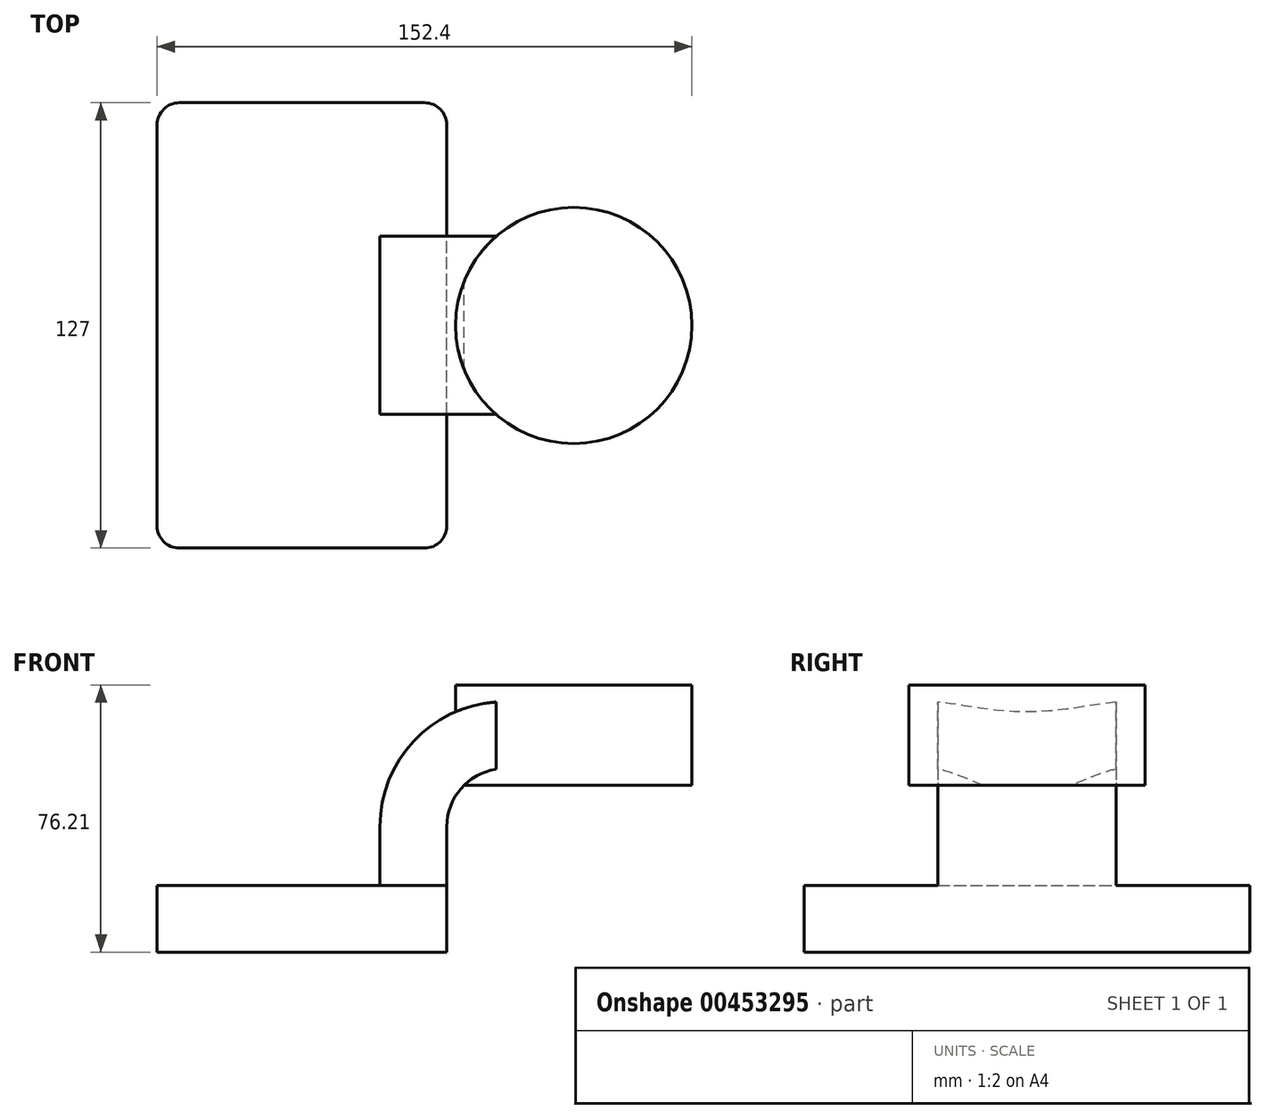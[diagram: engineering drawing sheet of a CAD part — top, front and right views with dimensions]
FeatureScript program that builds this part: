
annotation { "Feature Type Name" : "Feature", "Feature Type Description" : "" }
export const myFeature = defineFeature(function(context is Context, id is Id, definition is map)
    precondition{}
    {
        {
            var Q0;
            Q0=qCreatedBy(makeId("Front.planeOp"),FACE);
            var sketch = newSketch(context, id + "F0", { "sketchPlane" : qUnion([Q0])});
            skLineSegment(sketch, "E0.bottom", {"start": v(41.27, 9.53) * mm, "end": v(-41.27, 9.53) * mm});
            skLineSegment(sketch, "E0.top", {"start": v(41.27, -9.52) * mm, "end": v(-41.27, -9.52) * mm});
            skLineSegment(sketch, "E0.left", {"start": v(41.27, 9.53) * mm, "end": v(41.27, -9.52) * mm});
            skLineSegment(sketch, "E0.right", {"start": v(-41.27, 9.53) * mm, "end": v(-41.27, -9.52) * mm});
            skPoint(sketch, "E0.middle", {"position": v(0, 0) * mm});
            skLineSegment(sketch, "E1", {"start": v(41.27, 9.53) * mm, "end": v(41.27, 26.29) * mm});
            skArc(sketch, "E2", {"start": v(41.27, 26.29) * mm, "mid": v(46.11, 37.96) * mm, "end": v(57.78, 42.8) * mm});
            skLineSegment(sketch, "E3", {"start": v(57.78, 42.8) * mm, "end": v(77.45, 42.8) * mm});
            skLineSegment(sketch, "E4.bottom", {"start": v(111.12, 38.1) * mm, "end": v(60.32, 38.1) * mm});
            skLineSegment(sketch, "E4.top", {"start": v(111.12, 66.68) * mm, "end": v(60.32, 66.68) * mm});
            skLineSegment(sketch, "E4.left", {"start": v(111.12, 38.1) * mm, "end": v(111.12, 66.68) * mm});
            skLineSegment(sketch, "E4.right", {"start": v(60.32, 38.1) * mm, "end": v(60.32, 66.67) * mm});
            skPoint(sketch, "E4.middle", {"position": v(85.72, 52.39) * mm});
            skLineSegment(sketch, "E5.0", {"start": v(57.78, 61.85) * mm, "end": v(77.45, 61.85) * mm});
            skArc(sketch, "E5.1", {"start": v(22.22, 26.29) * mm, "mid": v(32.64, 51.43) * mm, "end": v(57.78, 61.85) * mm});
            skLineSegment(sketch, "E5.2", {"start": v(22.22, 9.53) * mm, "end": v(22.22, 26.29) * mm});
            skFitSpline(sketch, "E6", {"points": [v(-41.27, 9.53) * mm, v(57.78, 61.85) * mm], "startDerivative": vector(36.37, 117.55) * mm, "endDerivative": vector(119.29, -26.05) * mm});
            skLineSegment(sketch, "E7", {"start": v(77.45, 66.68) * mm, "end": v(77.45, 38.1) * mm});
            skSolve(sketch);
        }
        {
            var Q0;
            Q0=makeQuery(id+"F0.imprint","IMPRINT",FACE,{"disambiguationData":[TD([[makeQuery(id+"F0.imprint","IMPRINT",EDGE,{"derivedFrom":sQuery(id+"F0.wireOp",EDGE,"E0.top")}),-1.0]])]});
            extrude(context, id + "F1", {"entities" : qUnion([Q0]), "endBound" : BoundingType.SYMMETRIC, "depth" : 127 * mm});
        }
        {
            var Q0;
            {var subQ7=sQuery(id+"F0.wireOp",EDGE,"E1");Q0=makeQuery(id+"F0.imprint","IMPRINT",FACE,{"disambiguationData":[TD([[makeQuery(id+"F0.imprint","IMPRINT",EDGE,{"derivedFrom":subQ7}),1.0]])]});}
            var Q1;
            {var subQ0=sQuery(id+"F0.wireOp",EDGE,"E7");var subQ1=sQuery(id+"F0.wireOp",EDGE,"E3");var subQ2=makeQuery(id+"F0.imprint","INTERSECT",VERTEX,{"derivedFrom":[subQ1,subQ0]});Q1=makeQuery(id+"F0.imprint","IMPRINT",FACE,{"disambiguationData":[TD([[makeQuery(id+"F0.imprint","IMPRINT",EDGE,{"disambiguationData":[TD([[subQ2,1.0]])],"derivedFrom":subQ1}),1.0]])]});}
            extrude(context, id + "F2", {"entities" : qUnion([Q0, Q1]), "operationType" : NewBodyOperationType.ADD, "endBound" : BoundingType.SYMMETRIC, "depth" : 50.8 * mm});
        }
        {
            var Q0;
            Q0=makeQuery(id+"F0.imprint","IMPRINT",FACE,{"disambiguationData":[TD([[makeQuery(id+"F0.imprint","IMPRINT",EDGE,{"derivedFrom":sQuery(id+"F0.wireOp",EDGE,"E5.1")}),1.0]])]});
            extrude(context, id + "F3", {"entities" : qUnion([Q0]), "operationType" : NewBodyOperationType.ADD, "endBound" : BoundingType.SYMMETRIC, "depth" : 15.88 * mm});
        }
        {
            var Q0;
            {var subQ4=sQuery(id+"F0.wireOp",EDGE,"E4.left");Q0=makeQuery(id+"F0.imprint","IMPRINT",FACE,{"disambiguationData":[TD([[makeQuery(id+"F0.imprint","IMPRINT",EDGE,{"derivedFrom":subQ4}),1.0]])]});}
            var Q1;
            Q1=sQuery(id+"F0.wireOp",EDGE,"E7");
            revolve(context, id + "F4", {"operationType" : NewBodyOperationType.ADD, "entities" : qUnion([Q0]), "axis" : qUnion([Q1]), "revolveType" : RevolveType.FULL});
        }
        {
            var Q0;
            Q0=makeQuery(id+"F1.opExtrude","CAP_EDGE",EDGE,{"disambiguationData":[OSD([sQuery(id+"F0.wireOp",EDGE,"E0.left")])],"isStart":false});
            var Q1;
            Q1=makeQuery(id+"F1.opExtrude","CAP_EDGE",EDGE,{"disambiguationData":[OSD([sQuery(id+"F0.wireOp",EDGE,"E0.right")])],"isStart":false});
            var Q2;
            Q2=makeQuery(id+"F1.opExtrude","CAP_EDGE",EDGE,{"disambiguationData":[OSD([sQuery(id+"F0.wireOp",EDGE,"E0.left")])],"isStart":true});
            var Q3;
            Q3=makeQuery(id+"F1.opExtrude","CAP_EDGE",EDGE,{"disambiguationData":[OSD([sQuery(id+"F0.wireOp",EDGE,"E0.right")])],"isStart":true});
            fillet(context, id + "F5", {"entities" : qUnion([Q0, Q1, Q2, Q3]), "radius" : 6.35 * mm, "tangentPropagation" : true, "allowEdgeOverflow" : false});
        }
    });
